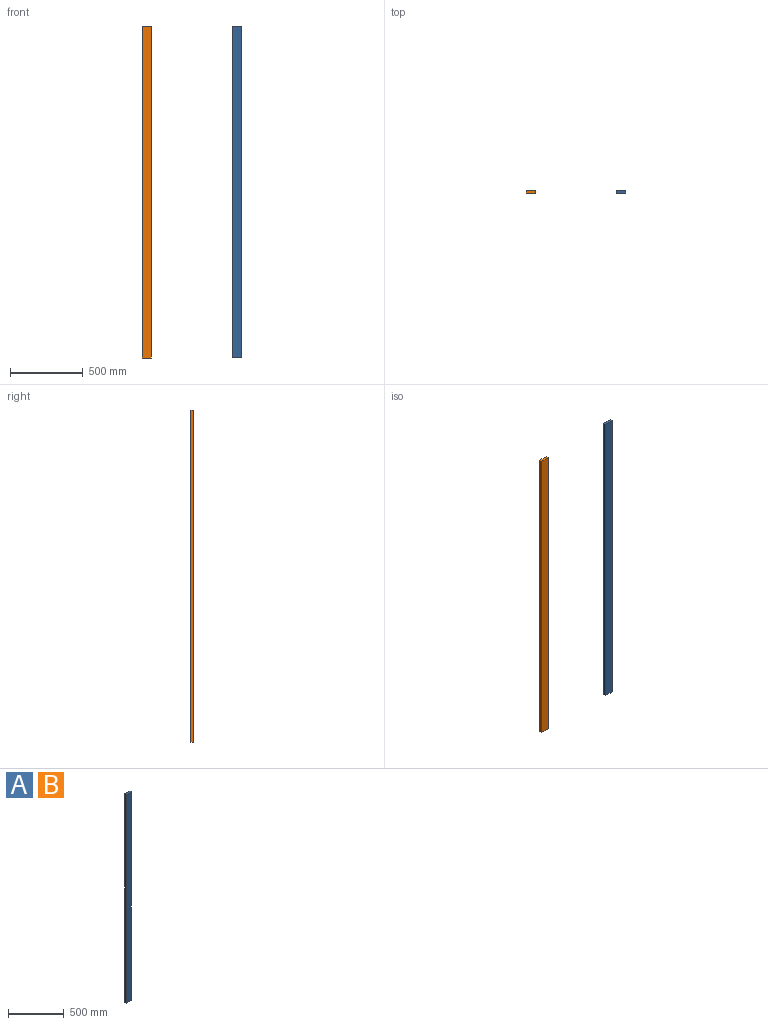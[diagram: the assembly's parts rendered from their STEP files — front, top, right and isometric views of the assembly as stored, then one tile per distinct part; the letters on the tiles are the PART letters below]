
ASSEMBLY  parts=2 mates=1
PART A: 6 faces, bbox 63.5x19.1x2286 mm
  f0: plane 2286x19.05mm, normal (1,0,0), area 43548.3mm2, adj f1,f3,f4,f5
  f1: plane 63.5x19.05mm, normal (0,0,1), area 1209.7mm2, adj f0,f2,f4,f5
  f2: plane 2286x19.05mm, normal (-1,0,0), area 43548.3mm2, adj f1,f3,f4,f5
  f3: plane 63.5x19.05mm, normal (0,0,-1), area 1209.7mm2, adj f0,f2,f4,f5
  f4: plane 2286x63.5mm, normal (0,-1,0), area 145161mm2, adj f0,f1,f2,f3
  f5: plane 2286x63.5mm, normal (0,1,0), area 145161mm2, adj f0,f1,f2,f3
PART B: same geometry as A
PLACE A t=(-3.93,-381.75,611.06)mm
PLACE B t=(-626.23,-381.75,611.06)mm
MATE planar A.f1 <-> B.f1  axis (0,0,1) through (-3.93,-391.27,1754.06)mm
